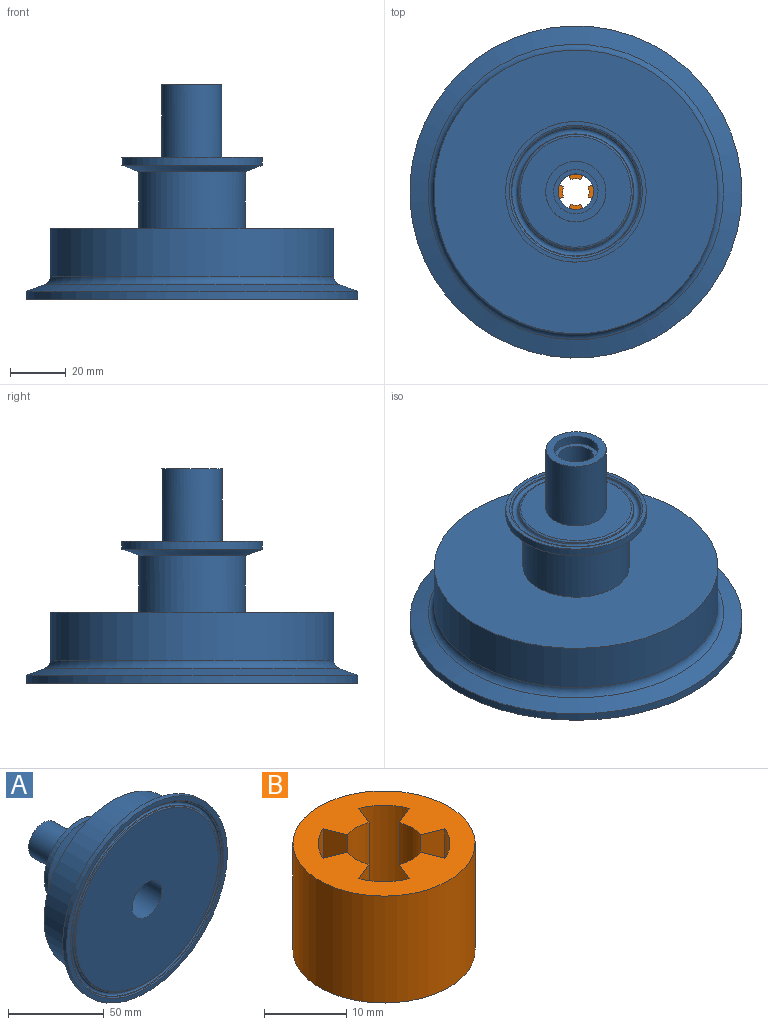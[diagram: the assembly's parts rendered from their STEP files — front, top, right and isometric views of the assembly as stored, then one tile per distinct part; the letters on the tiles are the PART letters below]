
ASSEMBLY  parts=2 mates=1
PART A: 29 faces, bbox 122.9x76.8x122.9 mm
  f0: cone r=14.79mm half-angle=70deg, axis (0,1,0), area 909.3mm2, adj f20,f26
  f1: cylinder r=50.8mm len=101.6mm, axis (0,-1,0), area 5483.5mm2, adj f9,f12
  f2: plane 118.92x118.92mm, normal (0,-1,0), area 975.3mm2, adj f3,f11
  f3: torus R=56.79mm, axis (0,-1,0), area 326.2mm2, adj f2,f4
  f4: cone r=56.07mm half-angle=23deg, axis (0,-1,0), area 150.2mm2, adj f3,f5
  f5: torus R=54.8mm, axis (0,-1,0), area 961.3mm2, adj f4,f6
  f6: cone r=53.7mm half-angle=23deg, axis (0,1,0), area 143.9mm2, adj f5,f7
  f7: torus R=52.81mm, axis (0,-1,0), area 307.9mm2, adj f6,f8
  f8: plane 105.62x105.62mm, normal (0,-1,0), area 8378mm2, adj f7,f25
  f9: torus R=53.98mm, axis (0,-1,0), area 1256mm2, adj f1,f10
  f10: cone r=52.89mm half-angle=70deg, axis (0,-1,0), area 2468.6mm2, adj f9,f11
  f11: cylinder r=59.46mm len=118.92mm, axis (0,-1,0), area 1062.8mm2, adj f2,f10
  f12: plane 101.6x101.6mm, normal (0,1,0), area 6967.2mm2, adj f1,f26
  f13: plane 50.39x50.39mm, normal (0,1,0), area 213.6mm2, adj f14,f20
  f14: torus R=23.81mm, axis (0,1,0), area 135.4mm2, adj f13,f15
  f15: cone r=23.08mm half-angle=23deg, axis (0,1,0), area 61.7mm2, adj f14,f16
  f16: torus R=21.82mm, axis (0,1,0), area 382.8mm2, adj f15,f17
  f17: cone r=20.72mm half-angle=23deg, axis (0,-1,0), area 55.4mm2, adj f16,f18
  f18: torus R=19.83mm, axis (0,1,0), area 117.1mm2, adj f17,f19
  f19: plane 39.66x39.66mm, normal (0,1,0), area 869mm2, adj f18,f28
  f20: cylinder r=25.2mm len=50.39mm, axis (0,1,0), area 450.4mm2, adj f0,f13
  f21: plane 21.59x21.59mm, normal (0,1,0), area 168.2mm2, adj f22,f28
  f22: cylinder r=7.94mm len=15.88mm, axis (0,1,0), area 158.3mm2, adj f21,f23
  f23: plane 15.88x15.88mm, normal (0,1,0), area 71.3mm2, adj f22,f27
  f24: plane 22.1x22.1mm, normal (0,-1,0), area 256.9mm2, adj f25,f27
  f25: cylinder r=11.05mm len=22.1mm, axis (0,1,0), area 1102.1mm2, adj f8,f24
  f26: cylinder r=19.05mm len=38.1mm, axis (0,-1,0), area 2432mm2, adj f0,f12
  f27: cylinder r=6.35mm len=57.79mm, axis (0,1,0), area 2305.5mm2, adj f23,f24
  f28: cylinder r=10.79mm len=26.04mm, axis (0,1,0), area 1765.9mm2, adj f19,f21
PART B: 19 faces, bbox 22.1x22.1x15.9 mm
  f0: plane 22.1x22.1mm, normal (0,0,1), area 247.3mm2, adj f2,f3,f4,f5,f6,f7,f8,f9
  f1: plane 22.1x22.1mm, normal (0,0,-1), area 247.3mm2, adj f2,f3,f4,f5,f6,f7,f8,f9
  f2: cylinder r=11.05mm len=22.1mm, axis (0,0,-1), area 1102.1mm2, adj f0,f1
  f3: plane 15.88x2.99mm, normal (0.38,-0.92,0), area 51.4mm2, adj f0,f1,f4,f18
  f4: cylinder r=8mm len=15.88mm, axis (0,0,1), area 99.8mm2, adj f0,f1,f3,f5
  f5: plane 15.88x2.99mm, normal (-0.92,0.38,0), area 51.4mm2, adj f0,f1,f4,f6
  f6: cylinder r=4.76mm len=15.88mm, axis (0,0,1), area 59.4mm2, adj f0,f1,f5,f7
  f7: plane 15.88x2.99mm, normal (0.92,0.38,0), area 51.4mm2, adj f0,f1,f6,f8
  f8: cylinder r=8mm len=15.88mm, axis (0,0,1), area 99.8mm2, adj f0,f1,f7,f9
  f9: plane 15.88x2.99mm, normal (-0.38,-0.92,0), area 51.4mm2, adj f0,f1,f8,f10
  f10: cylinder r=4.76mm len=15.88mm, axis (0,0,1), area 59.4mm2, adj f0,f1,f9,f11
  f11: plane 15.88x2.99mm, normal (-0.38,0.92,0), area 51.4mm2, adj f0,f1,f10,f12
  f12: cylinder r=8mm len=15.88mm, axis (0,0,1), area 99.8mm2, adj f0,f1,f11,f13
  f13: plane 15.88x2.99mm, normal (0.92,-0.38,0), area 51.4mm2, adj f0,f1,f12,f14
  f14: cylinder r=4.76mm len=15.88mm, axis (0,0,1), area 59.4mm2, adj f0,f1,f13,f15
  f15: plane 15.88x2.99mm, normal (-0.92,-0.38,0), area 51.4mm2, adj f0,f1,f14,f16
  f16: cylinder r=8mm len=15.88mm, axis (0,0,1), area 99.8mm2, adj f0,f1,f15,f17
  f17: plane 15.88x2.99mm, normal (0.38,0.92,0), area 51.4mm2, adj f0,f1,f16,f18
  f18: cylinder r=4.76mm len=15.88mm, axis (0,0,1), area 59.4mm2, adj f0,f1,f3,f17
PLACE A rot(axis=(1,0,0),90deg) t=(-70.05,-36.93,-2.66)mm
PLACE B t=(-70.05,-36.93,-2.66)mm
MATE fastened A.f0 <-> B.f2  axis (0,0,-1) through (-70.05,-36.93,13.21)mm
